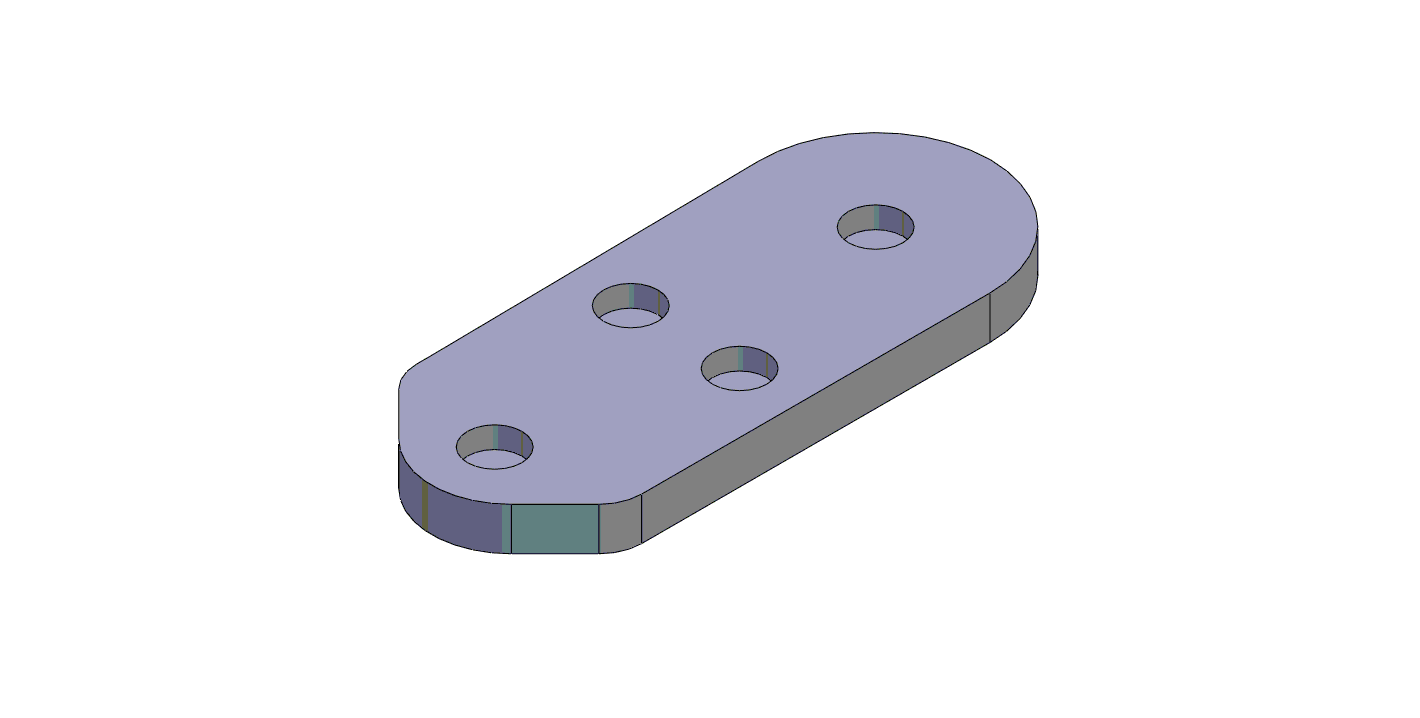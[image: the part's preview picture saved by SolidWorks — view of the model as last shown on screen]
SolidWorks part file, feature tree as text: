
SOLIDWORKS PART (.sldprt)
format: sldprt  version: not decoded by parser v0  size: 236,032 bytes
history: native  units: mm
features: sketch x7, extrude x4, cut_extrude x3, material x1, fillet x1 (+12 scaffold rows collapsed)
feature tree (28):
  scaffold x12  (default folders/planes/origin — collapsed)
  material  "Material <not specified>"
  sketch  "Sketch1"
  extrude  "Boss-Extrude1"  Depth=10mm
  sketch  "Sketch2"
  extrude  "Boss-Extrude2"  Depth=15mm
  fillet  "Fillet1"  Radius=1.27mm
  sketch  "Sketch3"
  cut_extrude  "Cut-Extrude5"  Depth=5mm
  sketch  "Sketch4"  dims[D1=~11.392321mm]
  cut_extrude  "Cut-Extrude6"  Depth=10mm
  sketch  "Sketch5"
  extrude  "Boss-Extrude3"  [1 undecoded]
  sketch  "Sketch6"  dims[D1=12.7mm]
  cut_extrude  "Cut-Extrude7"  [1 undecoded]
  sketch  "Sketch9"
  extrude  "Boss-Extrude4"  Depth=5mm
decode coverage: 8 of 15 modeling features carry decoded parameters
note: ~ marks probable driven/reference dimensions
note: 2 parameter values undecoded
note: suppression state not decoded; provenance and decode notes live in map.json
